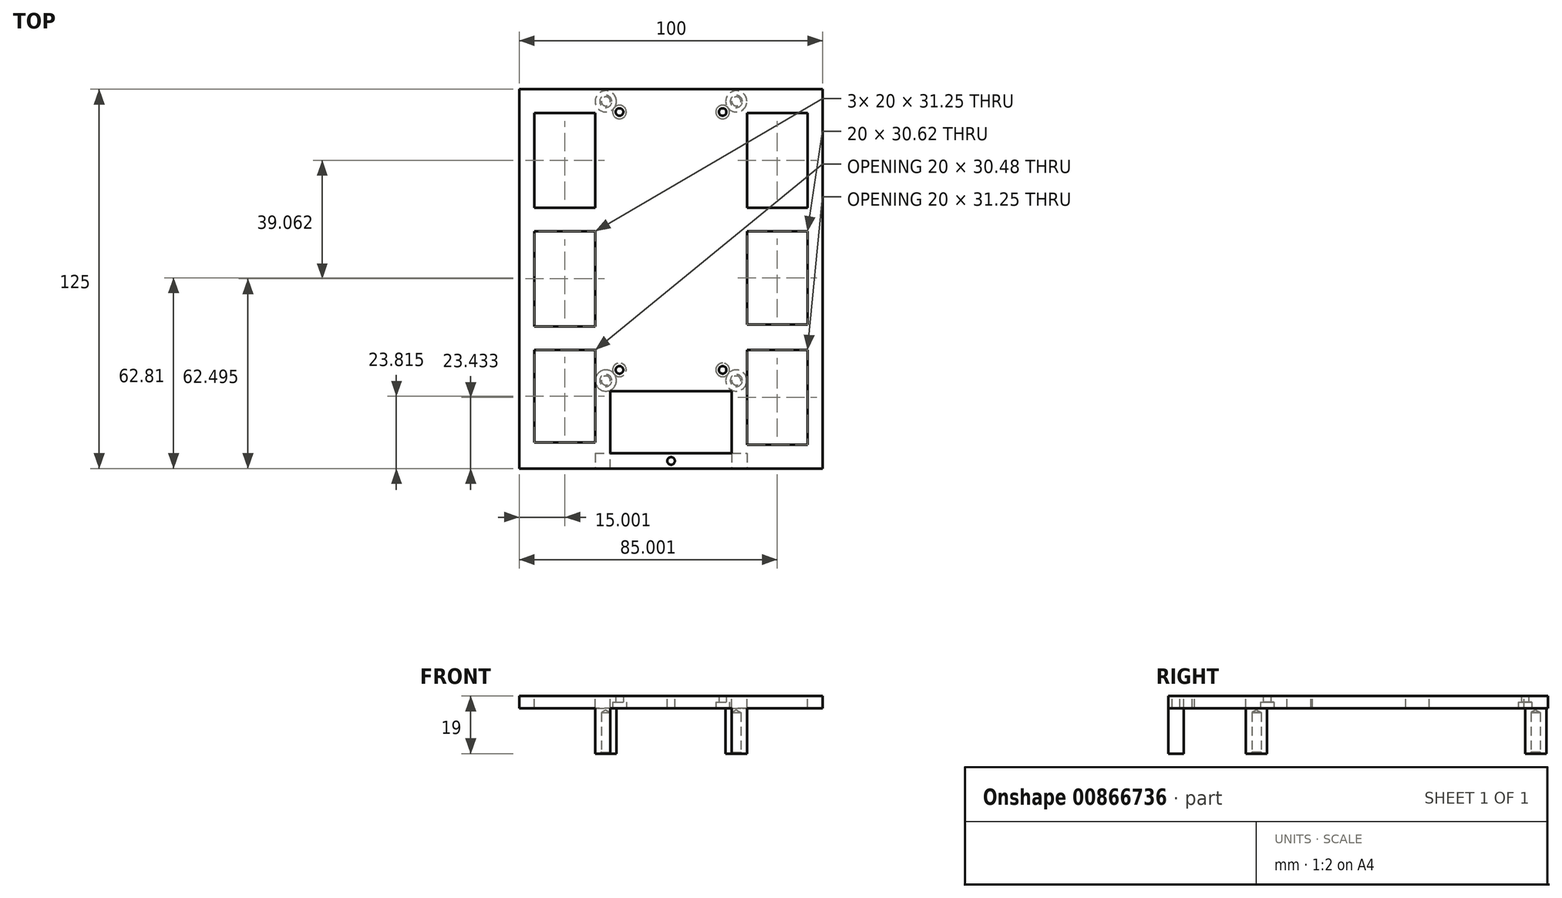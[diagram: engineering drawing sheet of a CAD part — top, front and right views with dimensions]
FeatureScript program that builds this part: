
annotation { "Feature Type Name" : "Feature", "Feature Type Description" : "" }
export const myFeature = defineFeature(function(context is Context, id is Id, definition is map)
    precondition{}
    {
        {
            assignVariable(context, id + "F0", {"name" : "RackThickness", "anyValue" : 4});
        }
        {
            assignVariable(context, id + "F1", {"name" : "PillarHeight", "anyValue" : 15});
        }
        {
            assignVariable(context, id + "F2", {"name" : "TailExtension", "anyValue" : 25});
        }
        {
            assignVariable(context, id + "F3", {"name" : "RackWidthExtension", "anyValue" : 25});
        }
        {
            var Q0;
            Q0=qCreatedBy(makeId("Top.planeOp"),FACE);
            var sketch = newSketch(context, id + "F4", { "sketchPlane" : qUnion([Q0])});
            skLineSegment(sketch, "E0.bottom", {"start": v(-22.43, 77.5) * mm, "end": v(27.57, 77.5) * mm});
            skLineSegment(sketch, "E0.top", {"start": v(-22.43, -22.5) * mm, "end": v(27.57, -22.5) * mm});
            skLineSegment(sketch, "E0.left", {"start": v(-22.43, 77.5) * mm, "end": v(-22.43, -22.5) * mm});
            skLineSegment(sketch, "E0.right", {"start": v(27.57, 77.5) * mm, "end": v(27.57, -22.5) * mm});
            skPoint(sketch, "E1", {"position": v(-14.43, 70) * mm});
            skPoint(sketch, "E2", {"position": v(19.57, 70) * mm});
            skPoint(sketch, "E3", {"position": v(19.57, -15) * mm});
            skPoint(sketch, "E4", {"position": v(-14.43, -15) * mm});
            skPoint(sketch, "E5", {"position": v(-18.93, -18.5) * mm});
            skPoint(sketch, "E6", {"position": v(24.07, -18.5) * mm});
            skPoint(sketch, "E7", {"position": v(24.07, 73.5) * mm});
            skPoint(sketch, "E8", {"position": v(-18.93, 73.5) * mm});
            skCircle(sketch, "E9", {"center": v(-18.93, 73.5) * mm, "radius": 3.5 * mm});
            skCircle(sketch, "E10", {"center": v(-18.93, -18.5) * mm, "radius": 3.5 * mm});
            skCircle(sketch, "E11", {"center": v(24.07, -18.5) * mm, "radius": 3.5 * mm});
            skCircle(sketch, "E12", {"center": v(24.07, 73.5) * mm, "radius": 3.5 * mm});
            skSolve(sketch);
        }
        {
            var Q0;
            Q0=makeQuery(id+"F4.imprint","IMPRINT",FACE,{"disambiguationData":[TD([[makeQuery(id+"F4.imprint","IMPRINT",EDGE,{"derivedFrom":sQuery(id+"F4.wireOp",EDGE,"E0.bottom")}),-1.0]])]});
            var Q1;
            Q1=makeQuery(id+"F4.imprint","IMPRINT",FACE,{"disambiguationData":[TD([[makeQuery(id+"F4.imprint","IMPRINT",EDGE,{"derivedFrom":sQuery(id+"F4.wireOp",EDGE,"E10")}),1.0]])]});
            var Q2;
            Q2=makeQuery(id+"F4.imprint","IMPRINT",FACE,{"disambiguationData":[TD([[makeQuery(id+"F4.imprint","IMPRINT",EDGE,{"derivedFrom":sQuery(id+"F4.wireOp",EDGE,"E11")}),1.0]])]});
            var Q3;
            Q3=makeQuery(id+"F4.imprint","IMPRINT",FACE,{"disambiguationData":[TD([[makeQuery(id+"F4.imprint","IMPRINT",EDGE,{"derivedFrom":sQuery(id+"F4.wireOp",EDGE,"E9")}),1.0]])]});
            var Q4;
            Q4=makeQuery(id+"F4.imprint","IMPRINT",FACE,{"disambiguationData":[TD([[makeQuery(id+"F4.imprint","IMPRINT",EDGE,{"derivedFrom":sQuery(id+"F4.wireOp",EDGE,"E12")}),1.0]])]});
            extrude(context, id + "F5", {"entities" : qUnion([Q0, Q1, Q2, Q3, Q4]), "depth" : (getVariable(context, 'RackThickness')) * mm, "offsetDistance" : 25 * mm});
        }
        {
            var Q0;
            Q0=sQuery(id+"F4.wireOp",VERTEX,"E2");
            var Q1;
            Q1=sQuery(id+"F4.wireOp",VERTEX,"E3");
            var Q2;
            Q2=sQuery(id+"F4.wireOp",VERTEX,"E4");
            var Q3;
            Q3=sQuery(id+"F4.wireOp",VERTEX,"E1");
            var Q4;
            Q4=makeQuery(id+"F5.opExtrude","SWEPT_BODY",BODY,{"disambiguationData":[OSD([sQuery(id+"F4.wireOp",EDGE,"E0.bottom"),sQuery(id+"F4.wireOp",EDGE,"E0.top"),sQuery(id+"F4.wireOp",EDGE,"E0.left"),sQuery(id+"F4.wireOp",EDGE,"E0.right")])]});
            hole(context, id + "F6", {"style" : HoleStyle.C_BORE, "endStyle" : HoleEndStyle.THROUGH, "oppositeDirection" : true, "holeDiameter" : 2.5 * mm, "cBoreDiameter" : 4.5 * mm, "cBoreDepth" : 2 * mm, "majorDiameter" : 5 * mm, "isTappedThrough" : true, "tappedDepth" : 12 * mm, "tapClearance" : 3, "startFromSketch" : true, "locations" : qUnion([Q0, Q1, Q2, Q3]), "scope" : qUnion([Q4])});
        }
        {
            var Q0;
            Q0=makeQuery(id+"F4.imprint","IMPRINT",FACE,{"disambiguationData":[TD([[makeQuery(id+"F4.imprint","IMPRINT",EDGE,{"derivedFrom":sQuery(id+"F4.wireOp",EDGE,"E10")}),1.0]])]});
            var Q1;
            Q1=makeQuery(id+"F4.imprint","IMPRINT",FACE,{"disambiguationData":[TD([[makeQuery(id+"F4.imprint","IMPRINT",EDGE,{"derivedFrom":sQuery(id+"F4.wireOp",EDGE,"E11")}),1.0]])]});
            var Q2;
            Q2=makeQuery(id+"F4.imprint","IMPRINT",FACE,{"disambiguationData":[TD([[makeQuery(id+"F4.imprint","IMPRINT",EDGE,{"derivedFrom":sQuery(id+"F4.wireOp",EDGE,"E9")}),1.0]])]});
            var Q3;
            Q3=makeQuery(id+"F4.imprint","IMPRINT",FACE,{"disambiguationData":[TD([[makeQuery(id+"F4.imprint","IMPRINT",EDGE,{"derivedFrom":sQuery(id+"F4.wireOp",EDGE,"E12")}),1.0]])]});
            extrude(context, id + "F7", {"entities" : qUnion([Q0, Q1, Q2, Q3]), "operationType" : NewBodyOperationType.ADD, "oppositeDirection" : true, "depth" : (getVariable(context, 'PillarHeight')) * mm, "offsetDistance" : 25 * mm});
        }
        {
            var Q0;
            Q0=makeQuery(id+"F7.opExtrude","CAP_FACE",FACE,{"disambiguationData":[OSD([sQuery(id+"F4.wireOp",EDGE,"E9")])],"isStart":false});
            var sketch = newSketch(context, id + "F8", { "sketchPlane" : qUnion([Q0])});
            skPoint(sketch, "E13", {"position": v(-18.93, -73.5) * mm});
            skSolve(sketch);
        }
        {
            var Q0;
            Q0=sQuery(id+"F8.wireOp",VERTEX,"E13");
            var Q1;
            Q1=makeQuery(id+"F5.opExtrude","SWEPT_BODY",BODY,{"disambiguationData":[OSD([sQuery(id+"F4.wireOp",EDGE,"E0.bottom"),sQuery(id+"F4.wireOp",EDGE,"E0.top"),sQuery(id+"F4.wireOp",EDGE,"E0.left"),sQuery(id+"F4.wireOp",EDGE,"E0.right")])]});
            hole(context, id + "F9", {"style" : HoleStyle.C_SINK, "endStyle" : HoleEndStyle.BLIND, "holeDiameter" : 3 * mm, "cSinkDiameter" : 4 * mm, "cSinkAngle" : 90 * degree, "majorDiameter" : 5 * mm, "holeDepth" : (.9 * getVariable(context, 'PillarHeight')) * mm, "isTappedThrough" : true, "tappedDepth" : 12 * mm, "tapClearance" : 3, "startFromSketch" : true, "locations" : qUnion([Q0]), "scope" : qUnion([Q1])});
        }
        {
            var Q0;
            Q0=makeQuery(id+"F7.opExtrude","CAP_FACE",FACE,{"disambiguationData":[OSD([sQuery(id+"F4.wireOp",EDGE,"E10")])],"isStart":false});
            var sketch = newSketch(context, id + "F10", { "sketchPlane" : qUnion([Q0])});
            skPoint(sketch, "E14", {"position": v(-18.93, 18.5) * mm});
            skSolve(sketch);
        }
        {
            var Q0;
            Q0=sQuery(id+"F10.wireOp",VERTEX,"E14");
            var Q1;
            Q1=makeQuery(id+"F5.opExtrude","SWEPT_BODY",BODY,{"disambiguationData":[OSD([sQuery(id+"F4.wireOp",EDGE,"E0.bottom"),sQuery(id+"F4.wireOp",EDGE,"E0.top"),sQuery(id+"F4.wireOp",EDGE,"E0.left"),sQuery(id+"F4.wireOp",EDGE,"E0.right")])]});
            hole(context, id + "F11", {"style" : HoleStyle.C_SINK, "endStyle" : HoleEndStyle.BLIND, "holeDiameter" : 3 * mm, "cSinkDiameter" : 4 * mm, "cSinkAngle" : 90 * degree, "majorDiameter" : 5 * mm, "holeDepth" : (.9 * getVariable(context, 'PillarHeight')) * mm, "isTappedThrough" : true, "tappedDepth" : 12 * mm, "tapClearance" : 3, "startFromSketch" : true, "locations" : qUnion([Q0]), "scope" : qUnion([Q1])});
        }
        {
            var Q0;
            Q0=makeQuery(id+"F7.opExtrude","CAP_FACE",FACE,{"disambiguationData":[OSD([sQuery(id+"F4.wireOp",EDGE,"E12")])],"isStart":false});
            var sketch = newSketch(context, id + "F12", { "sketchPlane" : qUnion([Q0])});
            skPoint(sketch, "E15", {"position": v(24.07, -73.5) * mm});
            skSolve(sketch);
        }
        {
            var Q0;
            Q0=sQuery(id+"F12.wireOp",VERTEX,"E15");
            var Q1;
            Q1=makeQuery(id+"F5.opExtrude","SWEPT_BODY",BODY,{"disambiguationData":[OSD([sQuery(id+"F4.wireOp",EDGE,"E0.bottom"),sQuery(id+"F4.wireOp",EDGE,"E0.top"),sQuery(id+"F4.wireOp",EDGE,"E0.left"),sQuery(id+"F4.wireOp",EDGE,"E0.right")])]});
            hole(context, id + "F13", {"style" : HoleStyle.C_SINK, "endStyle" : HoleEndStyle.BLIND, "holeDiameter" : 3 * mm, "cSinkDiameter" : 4 * mm, "cSinkAngle" : 90 * degree, "majorDiameter" : 5 * mm, "holeDepth" : (.9 * getVariable(context, 'PillarHeight')) * mm, "isTappedThrough" : true, "tappedDepth" : 12 * mm, "tapClearance" : 3, "startFromSketch" : true, "locations" : qUnion([Q0]), "scope" : qUnion([Q1])});
        }
        {
            var Q0;
            Q0=makeQuery(id+"F7.opExtrude","CAP_FACE",FACE,{"disambiguationData":[OSD([sQuery(id+"F4.wireOp",EDGE,"E11")])],"isStart":false});
            var sketch = newSketch(context, id + "F14", { "sketchPlane" : qUnion([Q0])});
            skPoint(sketch, "E16", {"position": v(24.07, 18.5) * mm});
            skSolve(sketch);
        }
        {
            var Q0;
            Q0=sQuery(id+"F14.wireOp",VERTEX,"E16");
            var Q1;
            Q1=makeQuery(id+"F5.opExtrude","SWEPT_BODY",BODY,{"disambiguationData":[OSD([sQuery(id+"F4.wireOp",EDGE,"E0.bottom"),sQuery(id+"F4.wireOp",EDGE,"E0.top"),sQuery(id+"F4.wireOp",EDGE,"E0.left"),sQuery(id+"F4.wireOp",EDGE,"E0.right")])]});
            hole(context, id + "F15", {"style" : HoleStyle.C_SINK, "endStyle" : HoleEndStyle.BLIND, "holeDiameter" : 3 * mm, "cSinkDiameter" : 4 * mm, "cSinkAngle" : 90 * degree, "majorDiameter" : 5 * mm, "holeDepth" : (.9 * getVariable(context, 'PillarHeight')) * mm, "isTappedThrough" : true, "tappedDepth" : 12 * mm, "tapClearance" : 3, "startFromSketch" : true, "locations" : qUnion([Q0]), "scope" : qUnion([Q1])});
        }
        {
            var Q0;
            Q0=makeQuery(id+"F5.opExtrude","SWEPT_FACE",FACE,{"disambiguationData":[OSD([sQuery(id+"F4.wireOp",EDGE,"E0.top")])]});
            extrude(context, id + "F16", {"entities" : qUnion([Q0]), "operationType" : NewBodyOperationType.ADD, "depth" : (getVariable(context, 'TailExtension')) * mm, "offsetDistance" : 25 * mm});
        }
        {
            var Q0;
            {var subQ0=sQuery(id+"F4.wireOp",EDGE,"E0.top");Q0=makeQuery(id+"F16.boolean.opBoolean","MERGE",FACE,{"derivedFrom":[makeQuery(id+"F5.opExtrude","CAP_FACE",FACE,{"disambiguationData":[OSD([sQuery(id+"F4.wireOp",EDGE,"E0.bottom"),subQ0,sQuery(id+"F4.wireOp",EDGE,"E0.left"),sQuery(id+"F4.wireOp",EDGE,"E0.right")])],"isStart":false}),makeQuery(id+"F16.opExtrude","SWEPT_FACE",FACE,{"disambiguationData":[OSD([subQ0]),TDD([makeQuery(id+"F5.opExtrude","CAP_EDGE",EDGE,{"disambiguationData":[OSD([subQ0])],"isStart":false})])]})]});}
            var sketch = newSketch(context, id + "F17", { "sketchPlane" : qUnion([Q0])});
            skLineSegment(sketch, "E17.bottom", {"start": v(22.57, -42.5) * mm, "end": v(-17.43, -42.5) * mm});
            skLineSegment(sketch, "E17.top", {"start": v(22.57, -22.05) * mm, "end": v(-17.43, -22.05) * mm});
            skLineSegment(sketch, "E17.left", {"start": v(22.57, -42.5) * mm, "end": v(22.57, -22.05) * mm});
            skLineSegment(sketch, "E17.right", {"start": v(-17.43, -42.5) * mm, "end": v(-17.43, -22.05) * mm});
            skPoint(sketch, "E18", {"position": v(2.57, -47.5) * mm});
            skPoint(sketch, "E19", {"position": v(2.57, -42.5) * mm});
            skLineSegment(sketch, "E20", {"start": v(2.57, -47.5) * mm, "end": v(2.57, -42.5) * mm});
            skPoint(sketch, "E21", {"position": v(2.57, -45) * mm});
            skCircle(sketch, "E22", {"center": v(2.57, -45) * mm, "radius": 1.25 * mm});
            skSolve(sketch);
        }
        {
            var Q0;
            Q0=makeQuery(id+"F17.imprint","IMPRINT",FACE,{"disambiguationData":[TD([[makeQuery(id+"F17.imprint","IMPRINT",EDGE,{"derivedFrom":sQuery(id+"F17.wireOp",EDGE,"E17.top")}),1.0]])]});
            var Q1;
            {var subQ0=sQuery(id+"F17.wireOp",EDGE,"E22");var subQ1=sQuery(id+"F17.wireOp",EDGE,"E20");var subQ2=makeQuery(id+"F17.imprint","INTERSECT",VERTEX,{"disambiguationData":[OD(0.0)],"derivedFrom":[subQ1,subQ0]});Q1=makeQuery(id+"F17.imprint","IMPRINT",FACE,{"disambiguationData":[TD([[makeQuery(id+"F17.imprint","IMPRINT",EDGE,{"disambiguationData":[TD([[subQ2,-1.0]])],"derivedFrom":subQ1}),1.0]])]});}
            var Q2;
            {var subQ0=sQuery(id+"F17.wireOp",EDGE,"E22");var subQ1=sQuery(id+"F17.wireOp",EDGE,"E20");var subQ2=makeQuery(id+"F17.imprint","INTERSECT",VERTEX,{"disambiguationData":[OD(0.0)],"derivedFrom":[subQ1,subQ0]});Q2=makeQuery(id+"F17.imprint","IMPRINT",FACE,{"disambiguationData":[TD([[makeQuery(id+"F17.imprint","IMPRINT",EDGE,{"disambiguationData":[TD([[subQ2,-1.0]])],"derivedFrom":subQ1}),-1.0]])]});}
            extrude(context, id + "F18", {"entities" : qUnion([Q0, Q1, Q2]), "operationType" : NewBodyOperationType.REMOVE, "oppositeDirection" : true, "depth" : (getVariable(context, 'RackThickness')) * mm, "offsetDistance" : 25 * mm});
        }
        {
            var Q0;
            {var subQ0=sQuery(id+"F4.wireOp",EDGE,"E0.top");Q0=makeQuery(id+"F16.boolean.opBoolean","MERGE",FACE,{"derivedFrom":[makeQuery(id+"F5.opExtrude","CAP_FACE",FACE,{"disambiguationData":[OSD([sQuery(id+"F4.wireOp",EDGE,"E0.bottom"),subQ0,sQuery(id+"F4.wireOp",EDGE,"E0.left"),sQuery(id+"F4.wireOp",EDGE,"E0.right")])],"isStart":true}),makeQuery(id+"F16.opExtrude","SWEPT_FACE",FACE,{"disambiguationData":[OSD([subQ0]),TDD([makeQuery(id+"F5.opExtrude","CAP_EDGE",EDGE,{"disambiguationData":[OSD([subQ0])],"isStart":true})])]})]});}
            var sketch = newSketch(context, id + "F19", { "sketchPlane" : qUnion([Q0])});
            skLineSegment(sketch, "E23.bottom", {"start": v(-22.43, 47.5) * mm, "end": v(-17.43, 47.5) * mm});
            skLineSegment(sketch, "E23.top", {"start": v(-22.43, 42.5) * mm, "end": v(-17.43, 42.5) * mm});
            skLineSegment(sketch, "E23.left", {"start": v(-22.43, 47.5) * mm, "end": v(-22.43, 42.5) * mm});
            skLineSegment(sketch, "E23.right", {"start": v(-17.43, 47.5) * mm, "end": v(-17.43, 42.5) * mm});
            skLineSegment(sketch, "E24.bottom", {"start": v(22.57, 42.5) * mm, "end": v(27.57, 42.5) * mm});
            skLineSegment(sketch, "E24.top", {"start": v(22.57, 47.5) * mm, "end": v(27.57, 47.5) * mm});
            skLineSegment(sketch, "E24.left", {"start": v(22.57, 42.5) * mm, "end": v(22.57, 47.5) * mm});
            skLineSegment(sketch, "E24.right", {"start": v(27.57, 42.5) * mm, "end": v(27.57, 47.5) * mm});
            skSolve(sketch);
        }
        {
            var Q0;
            {var subQ0=sQuery(id+"F4.wireOp",EDGE,"E0.right");Q0=makeQuery(id+"F16.boolean.opBoolean","MERGE",FACE,{"derivedFrom":[makeQuery(id+"F5.opExtrude","SWEPT_FACE",FACE,{"disambiguationData":[OSD([subQ0])]}),makeQuery(id+"F16.opExtrude","SWEPT_FACE",FACE,{"disambiguationData":[OSD([sQuery(id+"F4.wireOp",EDGE,"E0.top"),subQ0])]})]});}
            extrude(context, id + "F20", {"entities" : qUnion([Q0]), "operationType" : NewBodyOperationType.ADD, "depth" : (getVariable(context, 'RackWidthExtension')) * mm, "offsetDistance" : 25 * mm});
        }
        {
            var Q0;
            {var subQ0=sQuery(id+"F4.wireOp",EDGE,"E0.left");Q0=makeQuery(id+"F16.boolean.opBoolean","MERGE",FACE,{"derivedFrom":[makeQuery(id+"F5.opExtrude","SWEPT_FACE",FACE,{"disambiguationData":[OSD([subQ0])]}),makeQuery(id+"F16.opExtrude","SWEPT_FACE",FACE,{"disambiguationData":[OSD([sQuery(id+"F4.wireOp",EDGE,"E0.top"),subQ0])]})]});}
            extrude(context, id + "F21", {"entities" : qUnion([Q0]), "operationType" : NewBodyOperationType.ADD, "depth" : (getVariable(context, 'RackWidthExtension')) * mm, "offsetDistance" : 25 * mm});
        }
        {
            var Q0;
            {var subQ0=sQuery(id+"F4.wireOp",EDGE,"E0.left");var subQ1=sQuery(id+"F4.wireOp",EDGE,"E0.top");var subQ2=sQuery(id+"F4.wireOp",EDGE,"E0.right");Q0=makeQuery(id+"F21.boolean.opBoolean","MERGE",FACE,{"derivedFrom":[makeQuery(id+"F20.boolean.opBoolean","MERGE",FACE,{"derivedFrom":[makeQuery(id+"F16.boolean.opBoolean","MERGE",FACE,{"derivedFrom":[makeQuery(id+"F5.opExtrude","CAP_FACE",FACE,{"disambiguationData":[OSD([sQuery(id+"F4.wireOp",EDGE,"E0.bottom"),subQ1,subQ0,subQ2])],"isStart":false}),makeQuery(id+"F16.opExtrude","SWEPT_FACE",FACE,{"disambiguationData":[OSD([subQ1]),TDD([makeQuery(id+"F5.opExtrude","CAP_EDGE",EDGE,{"disambiguationData":[OSD([subQ1])],"isStart":false})])]})]}),makeQuery(id+"F20.opExtrude","SWEPT_FACE",FACE,{"disambiguationData":[OSD([subQ1,subQ2]),TDD([makeQuery(id+"F16.boolean.opBoolean","MERGE",EDGE,{"derivedFrom":[makeQuery(id+"F5.opExtrude","CAP_EDGE",EDGE,{"disambiguationData":[OSD([subQ2])],"isStart":false}),makeQuery(id+"F16.opExtrude","SWEPT_EDGE",EDGE,{"disambiguationData":[OSD([subQ1,subQ2]),TDD([makeQuery(id+"F5.opExtrude","CAP_VERTEX",VERTEX,{"disambiguationData":[OSD([subQ1,subQ2])],"isStart":false})])]})]})])]})]}),makeQuery(id+"F21.opExtrude","SWEPT_FACE",FACE,{"disambiguationData":[OSD([subQ1,subQ0]),TDD([makeQuery(id+"F16.boolean.opBoolean","MERGE",EDGE,{"derivedFrom":[makeQuery(id+"F5.opExtrude","CAP_EDGE",EDGE,{"disambiguationData":[OSD([subQ0])],"isStart":false}),makeQuery(id+"F16.opExtrude","SWEPT_EDGE",EDGE,{"disambiguationData":[OSD([subQ1,subQ0]),TDD([makeQuery(id+"F5.opExtrude","CAP_VERTEX",VERTEX,{"disambiguationData":[OSD([subQ1,subQ0])],"isStart":false})])]})]})])]})]});}
            var sketch = newSketch(context, id + "F22", { "sketchPlane" : qUnion([Q0])});
            skLineSegment(sketch, "E25.bottom", {"start": v(-42.43, 69.68) * mm, "end": v(-22.43, 69.68) * mm});
            skLineSegment(sketch, "E25.top", {"start": v(-42.43, 38.43) * mm, "end": v(-22.43, 38.43) * mm});
            skLineSegment(sketch, "E25.left", {"start": v(-42.43, 69.68) * mm, "end": v(-42.43, 38.43) * mm});
            skLineSegment(sketch, "E25.right", {"start": v(-22.43, 69.68) * mm, "end": v(-22.43, 38.43) * mm});
            skLineSegment(sketch, "E26.bottom", {"start": v(-42.43, 30.62) * mm, "end": v(-22.43, 30.62) * mm});
            skLineSegment(sketch, "E26.top", {"start": v(-42.43, -0.63) * mm, "end": v(-22.43, -0.63) * mm});
            skLineSegment(sketch, "E26.left", {"start": v(-42.43, 30.62) * mm, "end": v(-42.43, -0.63) * mm});
            skLineSegment(sketch, "E26.right", {"start": v(-22.43, 30.62) * mm, "end": v(-22.43, -0.63) * mm});
            skLineSegment(sketch, "E27.bottom", {"start": v(-42.43, -8.44) * mm, "end": v(-22.43, -8.44) * mm});
            skLineSegment(sketch, "E27.top", {"start": v(-42.43, -38.93) * mm, "end": v(-22.43, -38.93) * mm});
            skLineSegment(sketch, "E27.left", {"start": v(-42.43, -8.44) * mm, "end": v(-42.43, -38.93) * mm});
            skLineSegment(sketch, "E27.right", {"start": v(-22.43, -8.44) * mm, "end": v(-22.43, -38.93) * mm});
            skLineSegment(sketch, "E28.bottom", {"start": v(47.57, 69.68) * mm, "end": v(27.57, 69.68) * mm});
            skLineSegment(sketch, "E28.top", {"start": v(47.57, 38.43) * mm, "end": v(27.57, 38.43) * mm});
            skLineSegment(sketch, "E28.left", {"start": v(47.57, 69.68) * mm, "end": v(47.57, 38.43) * mm});
            skLineSegment(sketch, "E28.right", {"start": v(27.57, 69.68) * mm, "end": v(27.57, 38.43) * mm});
            skLineSegment(sketch, "E29.bottom", {"start": v(27.57, 30.62) * mm, "end": v(47.57, 30.62) * mm});
            skLineSegment(sketch, "E29.top", {"start": v(27.57, 0) * mm, "end": v(47.57, 0) * mm});
            skLineSegment(sketch, "E29.left", {"start": v(27.57, 30.62) * mm, "end": v(27.57, 0) * mm});
            skLineSegment(sketch, "E29.right", {"start": v(47.57, 30.62) * mm, "end": v(47.57, 0) * mm});
            skLineSegment(sketch, "E30.bottom", {"start": v(27.57, -8.44) * mm, "end": v(47.57, -8.44) * mm});
            skLineSegment(sketch, "E30.top", {"start": v(27.57, -39.7) * mm, "end": v(47.57, -39.7) * mm});
            skLineSegment(sketch, "E30.left", {"start": v(27.57, -8.44) * mm, "end": v(27.57, -39.7) * mm});
            skLineSegment(sketch, "E30.right", {"start": v(47.57, -8.44) * mm, "end": v(47.57, -39.7) * mm});
            skSolve(sketch);
        }
        {
            var Q0;
            Q0=makeQuery(id+"F22.imprint","IMPRINT",FACE,{"disambiguationData":[TD([[makeQuery(id+"F22.imprint","IMPRINT",EDGE,{"derivedFrom":sQuery(id+"F22.wireOp",EDGE,"E27.bottom")}),-1.0]])]});
            var Q1;
            Q1=makeQuery(id+"F22.imprint","IMPRINT",FACE,{"disambiguationData":[TD([[makeQuery(id+"F22.imprint","IMPRINT",EDGE,{"derivedFrom":sQuery(id+"F22.wireOp",EDGE,"E26.bottom")}),-1.0]])]});
            var Q2;
            Q2=makeQuery(id+"F22.imprint","IMPRINT",FACE,{"disambiguationData":[TD([[makeQuery(id+"F22.imprint","IMPRINT",EDGE,{"derivedFrom":sQuery(id+"F22.wireOp",EDGE,"E25.bottom")}),-1.0]])]});
            var Q3;
            Q3=makeQuery(id+"F22.imprint","IMPRINT",FACE,{"disambiguationData":[TD([[makeQuery(id+"F22.imprint","IMPRINT",EDGE,{"derivedFrom":sQuery(id+"F22.wireOp",EDGE,"E28.bottom")}),1.0]])]});
            var Q4;
            Q4=makeQuery(id+"F22.imprint","IMPRINT",FACE,{"disambiguationData":[TD([[makeQuery(id+"F22.imprint","IMPRINT",EDGE,{"derivedFrom":sQuery(id+"F22.wireOp",EDGE,"E29.bottom")}),-1.0]])]});
            var Q5;
            Q5=makeQuery(id+"F22.imprint","IMPRINT",FACE,{"disambiguationData":[TD([[makeQuery(id+"F22.imprint","IMPRINT",EDGE,{"derivedFrom":sQuery(id+"F22.wireOp",EDGE,"E30.bottom")}),-1.0]])]});
            extrude(context, id + "F23", {"entities" : qUnion([Q0, Q1, Q2, Q3, Q4, Q5]), "operationType" : NewBodyOperationType.REMOVE, "oppositeDirection" : true, "depth" : (getVariable(context, 'RackThickness')) * mm, "offsetDistance" : 25 * mm});
        }
        {
            var Q0;
            Q0=makeQuery(id+"F19.imprint","IMPRINT",FACE,{"disambiguationData":[TD([[makeQuery(id+"F19.imprint","IMPRINT",EDGE,{"derivedFrom":sQuery(id+"F19.wireOp",EDGE,"E23.bottom")}),-1.0]])]});
            var Q1;
            Q1=makeQuery(id+"F19.imprint","IMPRINT",FACE,{"disambiguationData":[TD([[makeQuery(id+"F19.imprint","IMPRINT",EDGE,{"derivedFrom":sQuery(id+"F19.wireOp",EDGE,"E24.bottom")}),1.0]])]});
            extrude(context, id + "F24", {"entities" : qUnion([Q0, Q1]), "operationType" : NewBodyOperationType.ADD, "depth" : (getVariable(context, 'PillarHeight')) * mm, "offsetDistance" : 25 * mm});
        }
    });
